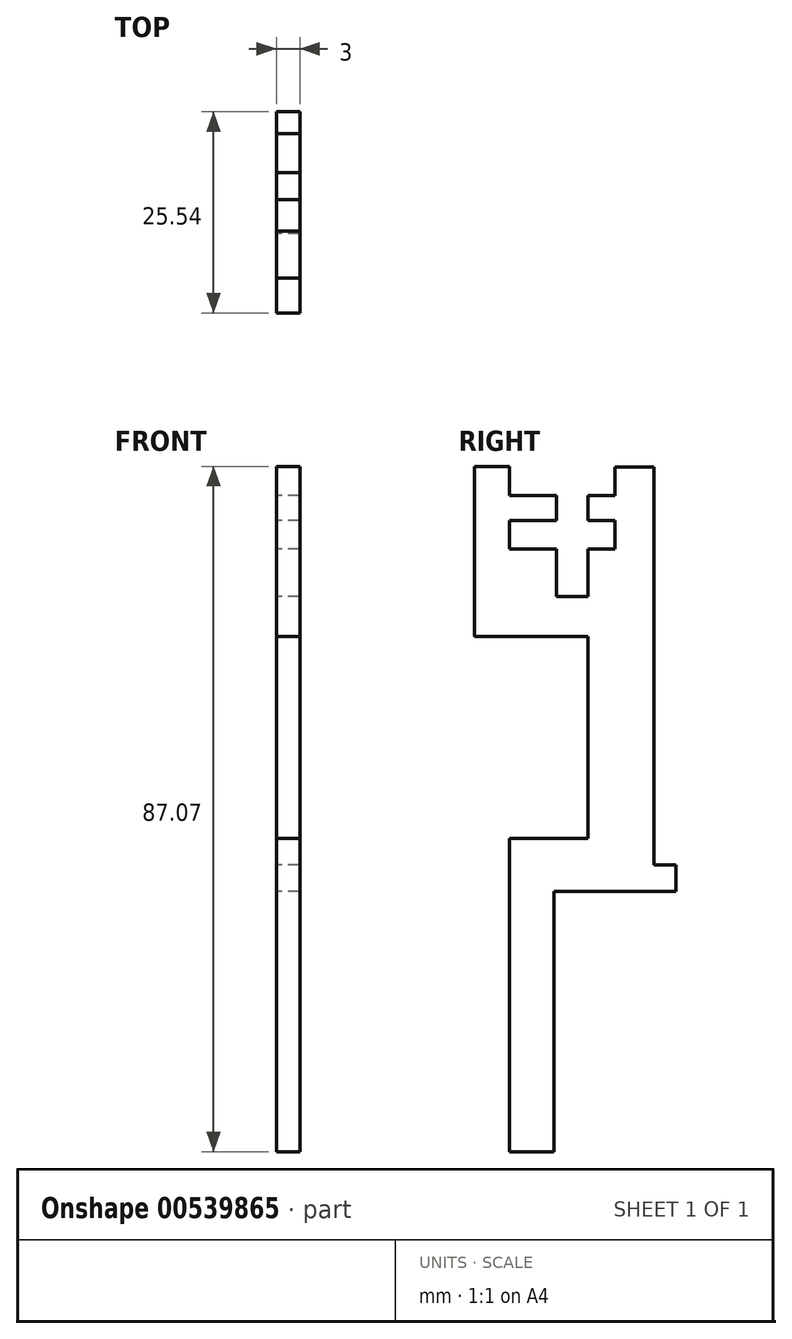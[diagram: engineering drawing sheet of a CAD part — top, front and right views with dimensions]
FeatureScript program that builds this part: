
annotation { "Feature Type Name" : "Feature", "Feature Type Description" : "" }
export const myFeature = defineFeature(function(context is Context, id is Id, definition is map)
    precondition{}
    {
        {
            var Q0;
            Q0=qCreatedBy(makeId("Right.planeOp"),FACE);
            var sketch = newSketch(context, id + "F0", { "sketchPlane" : qUnion([Q0])});
            skLineSegment(sketch, "E0.bottom", {"start": v(164.02, -96.44) * mm, "end": v(99.12, -96.44) * mm});
            skLineSegment(sketch, "E0.top", {"start": v(164.02, -55.2) * mm, "end": v(99.12, -55.2) * mm});
            skLineSegment(sketch, "E0.left", {"start": v(164.02, -55.2) * mm, "end": v(164.02, -96.44) * mm});
            skLineSegment(sketch, "E0.right", {"start": v(99.12, -55.2) * mm, "end": v(99.12, -96.44) * mm});
            skLineSegment(sketch, "E1", {"start": v(0, 0) * mm, "end": v(5.63, 0) * mm});
            skLineSegment(sketch, "E2", {"start": v(5.63, 0) * mm, "end": v(5.63, 33.05) * mm});
            skLineSegment(sketch, "E3", {"start": v(5.63, 33.05) * mm, "end": v(21.13, 33.05) * mm});
            skLineSegment(sketch, "E4", {"start": v(21.13, 33.05) * mm, "end": v(21.13, 36.42) * mm});
            skLineSegment(sketch, "E5", {"start": v(21.13, 36.42) * mm, "end": v(18.36, 36.42) * mm});
            skLineSegment(sketch, "E6", {"start": v(18.36, 36.42) * mm, "end": v(18.36, 86.98) * mm});
            skLineSegment(sketch, "E7", {"start": v(18.36, 86.98) * mm, "end": v(13.38, 86.98) * mm});
            skPoint(sketch, "E7.endSnap0", {"position": v(13.38, 33.05) * mm});
            skLineSegment(sketch, "E8", {"start": v(13.38, 86.98) * mm, "end": v(13.38, 83.37) * mm});
            skLineSegment(sketch, "E9", {"start": v(13.38, 83.37) * mm, "end": v(10, 83.37) * mm});
            skLineSegment(sketch, "E10", {"start": v(10, 83.37) * mm, "end": v(10, 80.17) * mm});
            skLineSegment(sketch, "E11", {"start": v(10, 80.17) * mm, "end": v(13.38, 80.17) * mm});
            skLineSegment(sketch, "E12", {"start": v(13.38, 80.17) * mm, "end": v(13.38, 76.56) * mm});
            skLineSegment(sketch, "E13", {"start": v(13.38, 76.56) * mm, "end": v(10, 76.56) * mm});
            skLineSegment(sketch, "E14", {"start": v(10, 76.56) * mm, "end": v(10, 70.55) * mm});
            skLineSegment(sketch, "E15", {"start": v(10, 70.55) * mm, "end": v(5.99, 70.55) * mm});
            skLineSegment(sketch, "E16", {"start": v(5.99, 70.55) * mm, "end": v(5.99, 76.56) * mm});
            skLineSegment(sketch, "E17", {"start": v(5.99, 76.56) * mm, "end": v(0, 76.56) * mm});
            skLineSegment(sketch, "E18", {"start": v(0, 76.56) * mm, "end": v(0, 80.17) * mm});
            skLineSegment(sketch, "E19", {"start": v(0, 80.17) * mm, "end": v(5.99, 80.17) * mm});
            skLineSegment(sketch, "E20", {"start": v(5.99, 80.17) * mm, "end": v(5.99, 83.37) * mm});
            skLineSegment(sketch, "E21", {"start": v(5.99, 83.37) * mm, "end": v(0, 83.37) * mm});
            skLineSegment(sketch, "E22", {"start": v(0, 83.37) * mm, "end": v(0, 87.07) * mm});
            skLineSegment(sketch, "E23", {"start": v(0, 87.07) * mm, "end": v(-4.4, 87.07) * mm});
            skLineSegment(sketch, "E24", {"start": v(-4.4, 87.07) * mm, "end": v(-4.4, 65.47) * mm});
            skLineSegment(sketch, "E25", {"start": v(-4.4, 65.47) * mm, "end": v(10, 65.47) * mm});
            skLineSegment(sketch, "E26", {"start": v(10, 65.47) * mm, "end": v(10, 39.78) * mm});
            skLineSegment(sketch, "E27", {"start": v(10, 39.78) * mm, "end": v(0, 39.78) * mm});
            skLineSegment(sketch, "E28", {"start": v(0, 39.78) * mm, "end": v(0, 0) * mm});
            skSolve(sketch);
        }
        {
            var Q0;
            Q0=makeQuery(id+"F0.imprint","IMPRINT",FACE,{"disambiguationData":[TD([[makeQuery(id+"F0.imprint","IMPRINT",EDGE,{"derivedFrom":sQuery(id+"F0.wireOp",EDGE,"E1")}),1.0]])]});
            extrude(context, id + "F1", {"entities" : qUnion([Q0]), "depth" : 3 * mm, "offsetDistance" : 25 * mm});
        }
    });
